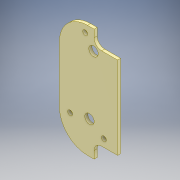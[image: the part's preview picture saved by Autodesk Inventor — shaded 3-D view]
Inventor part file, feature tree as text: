
AUTODESK INVENTOR PART (.ipt)
format: ipt  version: 2019 (Build 230136000, 136)  size: 158,720 bytes
history: native  units: mm
features: extrude x3, sketch x3, other x1, fillet x1
ambient origin geometry x8: Origin, YZ Plane, XZ Plane, XY Plane, X Axis, Y Axis, Z Axis, Center Point
bodies: Solide1 (feature_tree)
feature tree (8):
  other  "PCB Droit"
  extrude  "Extrusion1"  Depth=31.0mm
  fillet  "Congé1"  Radius=60.0mm
  extrude  "Extrusion3"  Depth=30.0mm
  extrude  "Extrusion4"  Depth=15.5mm
  sketch  "Esquisse1"
  sketch  "Esquisse2"
  sketch  "Esquisse3"
